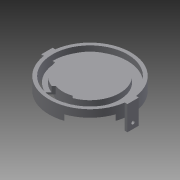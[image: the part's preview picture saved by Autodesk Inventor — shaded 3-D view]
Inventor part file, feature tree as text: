
AUTODESK INVENTOR PART (.ipt)
format: ipt  version: 2015 SP2 (Build 190223200, 223)  size: 247,296 bytes
history: native  units: in
note: dims shown in document units (in); Inventor stores cm internally (conversion verified against a paired STEP export)
features: sketch x13, extrude x11, hole x2, thread x1
ambient origin geometry x8: Origin, YZ Plane, XZ Plane, XY Plane, X Axis, Y Axis, Z Axis, Center Point
bodies: Solid1 (feature_tree)
feature tree (27):
  extrude  "Extrusion1"  Depth=2.5984in
  extrude  "Extrusion2"  Depth=0.0591in
  extrude  "Extrusion3"  TaperAngle=45.0deg  [1 undecoded]
  extrude  "Extrusion8"  Depth=0.2953in
  extrude  "Extrusion13"  Depth=0.0591in TaperAngle=0.0deg
  extrude  "Extrusion14"  TaperAngle=180.0deg  [1 undecoded]
  extrude  "Extrusion15"  Depth=0.3937in
  thread  "Thread1"  [1 undecoded]
  extrude  "Extrusion16"  Depth=0.315in
  extrude  "Extrusion17"  Depth=0.2559in TaperAngle=0.0deg
  extrude  "Extrusion18"  Depth=2.8346in
  extrude  "Extrusion19"  Depth=0.1969in TaperAngle=0.0deg
  hole  "Hole3"  [1 undecoded]
  hole  "Hole4"  [1 undecoded]
  sketch  "Sketch1"  dims[d0=2.0669in d1=2.5984in]
  sketch  "Sketch2"  dims[d2=0.0591in d3=0.0in d4=1.9685in]
  sketch  "Sketch3"  dims[d5=135.0deg d6=45.0deg]
  sketch  "Sketch8"  dims[d7=0.5906in d9=0.2953in]
  sketch  "Sketch16"  dims[d10=0.0in d11=0.0591in d12=0.0in]
  sketch  "Sketch19"  dims[d13=2.3622in d14=180.0deg]
  sketch  "Sketch20"  dims[d15=0.3937in d16=0.0in d29=2.5984in d30=0.1181in]
  sketch  "Sketch21"  dims[d31=0.2559in d32=0.0in d66=0.315in]
  sketch  "Sketch23"  dims[d67=2.0669in d68=0.2559in d69=0.0in]
  sketch  "Sketch24"  dims[d70=1.8898in d71=135.0deg d72=45.0deg d73=0.5906in d74=0.2953in d75=0.0in d76=0.3543in d77=0.2559in d78=0.0in d81=2.8346in]
  sketch  "Sketch25"  dims[d82=0.1181in d83=0.1969in d84=0.0in]
  sketch  "Sketch26"  dims[d85=0.1969in d86=0.2559in d87=1.7717in]
  sketch  "Sketch27"  dims[d88=0.0394in d89=0.1575in d90=0.0in d91=2.8346in d94=0.1969in d95=0.0in d96=1.7717in d97=0.0787in d98=0.0in d99=0.3937in d100=0.1969in d101=1.4961in d102=1.4961in d103=0.3937in d104=0.4528in d105=0.0in d106=0.0in d107=1.4961in d108=0.1181in d110=0.3937in d112=0.1969in d113=0.1181in d114=0.2362in d115=0.1575in d116=0.0787in d117=90.0deg d118=0.315in d119=0.8108in d120=0.3937in d121=0.1181in d122=0.1969in d123=0.3937in d124=0.1969in d125=0.1181in d126=0.2362in d127=0.1575in d128=0.0787in d129=90.0deg d130=0.315in d131=0.8108in d132=0.1969in d133=2.8346in d134=2.5984in d135=0.6496in d136=0.8465in d137=0.1969in d138=2.5984in]
note: 5 required parameter values undecoded (feature->parameter linkage not recoverable at this tier; creation-order binding heuristic only, values carry confidence <= 0.55)
